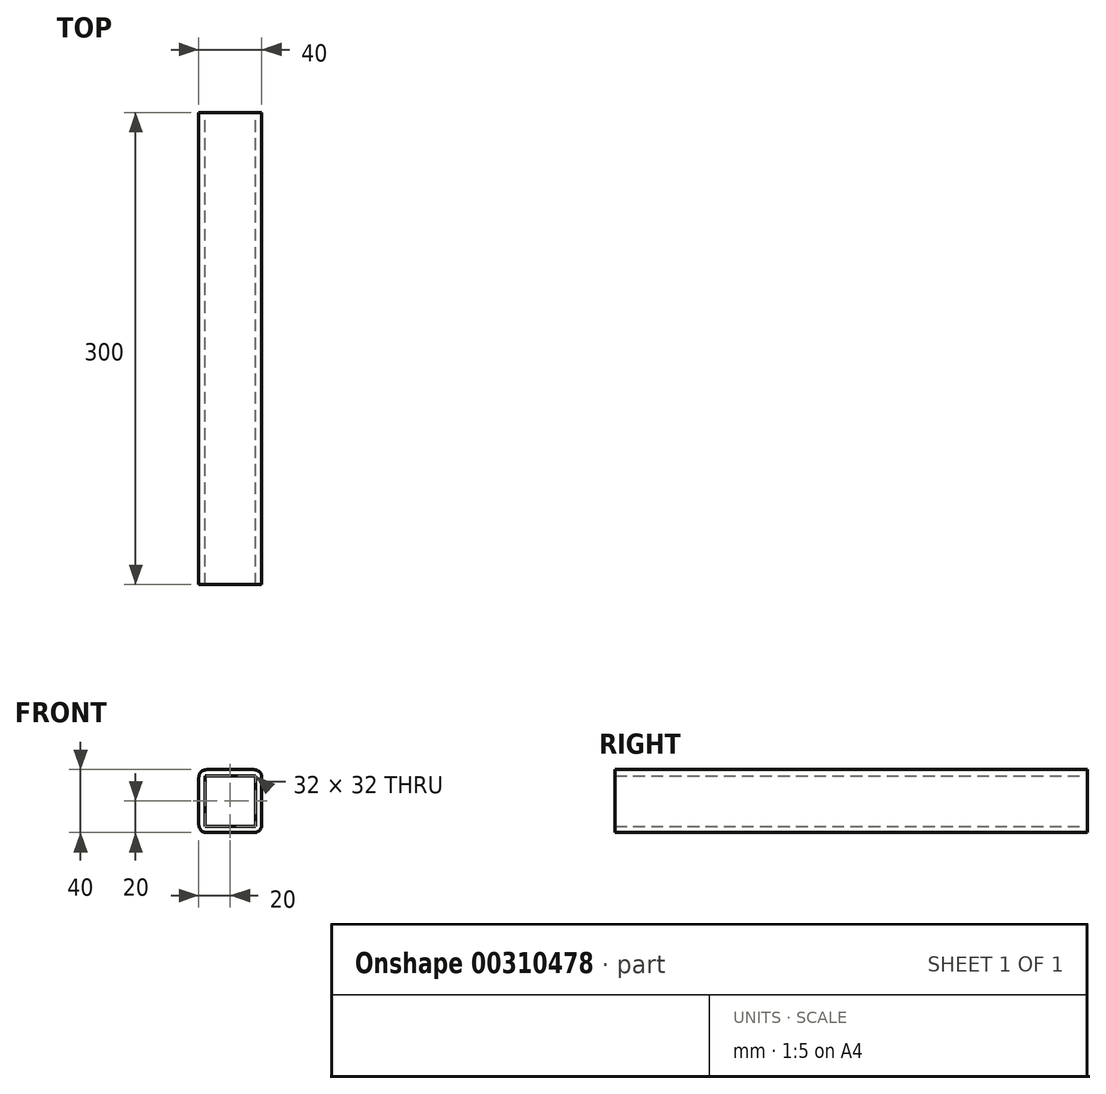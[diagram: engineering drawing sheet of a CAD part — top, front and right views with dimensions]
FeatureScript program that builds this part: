
annotation { "Feature Type Name" : "Feature", "Feature Type Description" : "" }
export const myFeature = defineFeature(function(context is Context, id is Id, definition is map)
    precondition{}
    {
        {
            var Q0;
            Q0=qCreatedBy(makeId("Front.planeOp"),FACE);
            var sketch = newSketch(context, id + "F0", { "sketchPlane" : qUnion([Q0])});
            skLineSegment(sketch, "E0.bottom", {"start": v(15, -20) * mm, "end": v(-15, -20) * mm});
            skLineSegment(sketch, "E0.top", {"start": v(15, 20) * mm, "end": v(-15, 20) * mm});
            skLineSegment(sketch, "E0.left", {"start": v(20, -15) * mm, "end": v(20, 15) * mm});
            skLineSegment(sketch, "E0.right", {"start": v(-20, -15) * mm, "end": v(-20, 15) * mm});
            skPoint(sketch, "E0.middle", {"position": v(0, 0) * mm});
            skPoint(sketch, "E1.visualSharp", {"position": v(-20, 20) * mm});
            skArc(sketch, "E1.filletArc", {"start": v(-15, 20) * mm, "mid": v(-18.54, 18.54) * mm, "end": v(-20, 15) * mm});
            skPoint(sketch, "E2.visualSharp", {"position": v(20, 20) * mm});
            skArc(sketch, "E2.filletArc", {"start": v(20, 15) * mm, "mid": v(18.54, 18.54) * mm, "end": v(15, 20) * mm});
            skPoint(sketch, "E3.visualSharp", {"position": v(20, -20) * mm});
            skArc(sketch, "E3.filletArc", {"start": v(15, -20) * mm, "mid": v(18.54, -18.54) * mm, "end": v(20, -15) * mm});
            skPoint(sketch, "E4.visualSharp", {"position": v(-20, -20) * mm});
            skArc(sketch, "E4.filletArc", {"start": v(-20, -15) * mm, "mid": v(-18.54, -18.54) * mm, "end": v(-15, -20) * mm});
            skLineSegment(sketch, "E5.0", {"start": v(-16, -16) * mm, "end": v(-16, 16) * mm});
            skLineSegment(sketch, "E5.1", {"start": v(16, -16) * mm, "end": v(-16, -16) * mm});
            skLineSegment(sketch, "E5.2", {"start": v(16, -16) * mm, "end": v(16, 16) * mm});
            skLineSegment(sketch, "E5.3", {"start": v(16, 16) * mm, "end": v(-16, 16) * mm});
            skSolve(sketch);
        }
        {
            var Q0;
            Q0=makeQuery(id+"F0.imprint","IMPRINT",FACE,{"disambiguationData":[TD([[makeQuery(id+"F0.imprint","IMPRINT",EDGE,{"derivedFrom":sQuery(id+"F0.wireOp",EDGE,"E0.bottom")}),-1.0]])]});
            extrude(context, id + "F1", {"entities" : qUnion([Q0]), "depth" : 300 * mm});
        }
    });
